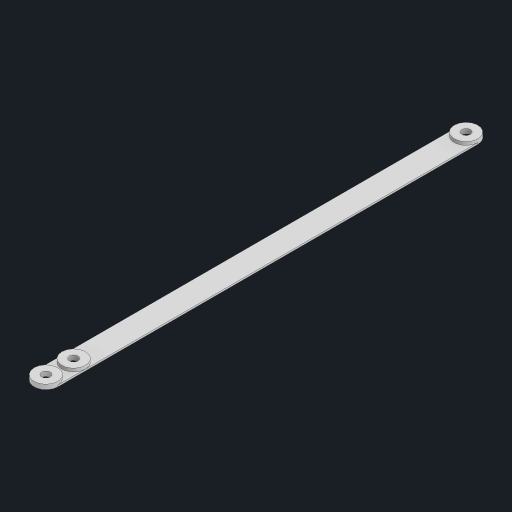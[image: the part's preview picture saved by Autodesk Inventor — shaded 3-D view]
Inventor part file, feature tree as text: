
AUTODESK INVENTOR PART (.ipt)
format: ipt  version: 2023 (Build 270158000, 158)  size: 117,760 bytes
history: native  units: mm
features: extrude x2, sketch x1
ambient origin geometry x8: Origin, YZ Plane, XZ Plane, XY Plane, X Axis, Y Axis, Z Axis, Center Point
bodies: Solid1 (feature_tree)
feature tree (3):
  sketch  "Sketch1"  dims[d0=15.0mm d1=5.5mm d7=15.0mm d10=3.0mm d11=0.0mm d12=15.0mm d13=5.5mm d14=1.0mm d15=0.0mm d17=262.97mm d18=15.0mm d19=2.5mm d22=15.0mm d23=5.5mm d24=0.5mm d25=0.872665mm d26=0.5mm d27=0.872665mm]
  extrude  "Extrusion2"  Depth=15.0mm
  extrude  "Extrusion3"  Depth=15.0mm
